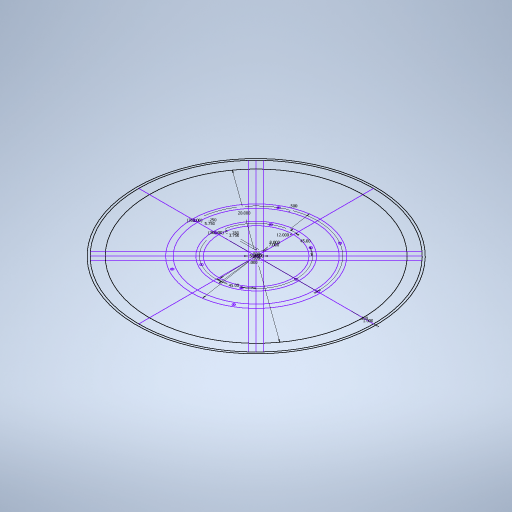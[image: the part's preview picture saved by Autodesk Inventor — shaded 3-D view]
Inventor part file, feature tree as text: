
AUTODESK INVENTOR PART (.ipt)
format: ipt  version: 2023 (Build 270158000, 158)  size: 265,728 bytes
history: native  units: in
note: dims shown in document units (in); Inventor stores cm internally (conversion verified against a paired STEP export)
features: sketch x1
ambient origin geometry x8: Origin, YZ Plane, XZ Plane, XY Plane, X Axis, Y Axis, Z Axis, Center Point
feature tree (1):
  sketch  "Sketch1"  dims[d0=20.0in d1=1.0in d2=45.0deg d3=0.0in d4=0.0in d5=45.0deg d6=0.5in d7=0.5in d8=0.5in d9=0.5in d10=12.0in d11=8.0in d12=7.0in d13=0.5in d14=0.25in d15=5.75in d16=2.3622in d18=360.0deg d20=0.25in d21=3.75in d22=2.3622in d24=360.0deg d26=0.2in]
